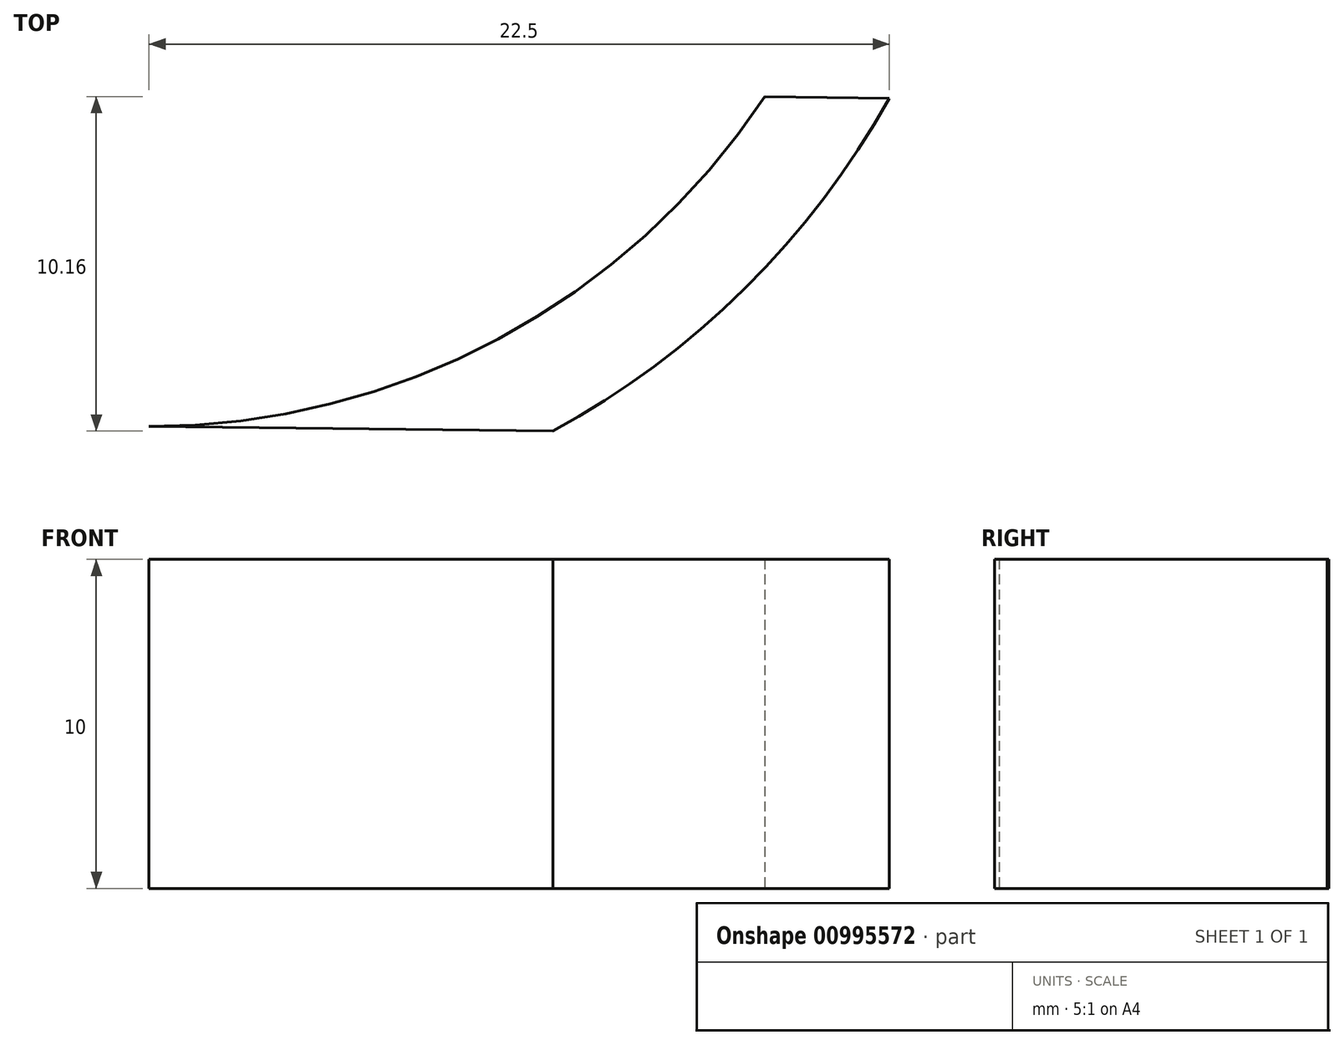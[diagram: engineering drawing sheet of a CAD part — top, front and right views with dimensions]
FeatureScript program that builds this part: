
annotation { "Feature Type Name" : "Feature", "Feature Type Description" : "" }
export const myFeature = defineFeature(function(context is Context, id is Id, definition is map)
    precondition{}
    {
        {
            var Q0;
            Q0=qCreatedBy(makeId("Top.planeOp"),FACE);
            var sketch = newSketch(context, id + "F0", { "sketchPlane" : qUnion([Q0])});
            skLineSegment(sketch, "E0", {"start": v(-15.96, 20.32) * mm, "end": v(-15.96, -25.18) * mm, "construction": true});
            skPoint(sketch, "E1", {"position": v(-15.96, -2.43) * mm});
            skLineSegment(sketch, "E2", {"start": v(70.17, -2.43) * mm, "end": v(-91.58, -2.43) * mm, "construction": true});
            skLineSegment(sketch, "E3", {"start": v(-15.96, -2.43) * mm, "end": v(-38.46, -2.43) * mm, "construction": true});
            skCircle(sketch, "E4", {"center": v(-38.46, -2.43) * mm, "radius": 22.5 * mm, "construction": true});
            skLineSegment(sketch, "E5", {"start": v(-38.46, -2.43) * mm, "end": v(-38.46, 20.07) * mm, "construction": true});
            skLineSegment(sketch, "E6", {"start": v(-38.46, -2.43) * mm, "end": v(-38.46, -24.93) * mm, "construction": true});
            skArc(sketch, "E7", {"start": v(-38.46, 23.32) * mm, "mid": v(-56.67, 15.77) * mm, "end": v(-64.21, -2.43) * mm});
            skArc(sketch, "E8", {"start": v(-38.46, 20.07) * mm, "mid": v(-54.37, 13.48) * mm, "end": v(-60.96, -2.43) * mm});
            skArc(sketch, "E9", {"start": v(-38.46, 23.32) * mm, "mid": v(-32.13, 22.53) * mm, "end": v(-26.2, 20.2) * mm, "construction": true});
            skArc(sketch, "E10", {"start": v(-26.2, 20.2) * mm, "mid": v(-20.36, 15.87) * mm, "end": v(-15.96, 10.09) * mm});
            skLineSegment(sketch, "E11", {"start": v(-15.96, 10.09) * mm, "end": v(-19.74, 10.05) * mm});
            skArc(sketch, "E12", {"start": v(-38.46, 20.07) * mm, "mid": v(-27.85, 17.4) * mm, "end": v(-19.74, 10.05) * mm});
            skArc(sketch, "E13.MirrorCS", {"start": v(-38.46, -28.18) * mm, "mid": v(-56.67, -20.64) * mm, "end": v(-64.21, -2.43) * mm});
            skArc(sketch, "E14.MirrorCS", {"start": v(-38.46, -24.93) * mm, "mid": v(-54.37, -18.34) * mm, "end": v(-60.96, -2.43) * mm});
            skArc(sketch, "E15.MirrorCS", {"start": v(-38.46, -24.93) * mm, "mid": v(-27.85, -22.27) * mm, "end": v(-19.74, -14.91) * mm});
            skLineSegment(sketch, "E16.MirrorCS", {"start": v(4.39, -28.18) * mm, "end": v(-38.46, -28.18) * mm});
            skArc(sketch, "E17.MirrorCS", {"start": v(-26.2, -25.07) * mm, "mid": v(-20.36, -20.74) * mm, "end": v(-15.96, -14.96) * mm});
            skLineSegment(sketch, "E18.MirrorCS", {"start": v(-15.96, -25.18) * mm, "end": v(-38.46, -24.93) * mm});
            skLineSegment(sketch, "E19.MirrorCS", {"start": v(-15.96, -14.96) * mm, "end": v(-19.74, -14.91) * mm});
            skLineSegment(sketch, "E20.MirrorCS", {"start": v(1.04, -25.18) * mm, "end": v(-15.96, -25.18) * mm});
            skLineSegment(sketch, "E21.MirrorCS", {"start": v(1.04, -22.18) * mm, "end": v(1.04, -25.18) * mm});
            skLineSegment(sketch, "E22.MirrorCS", {"start": v(4.39, -25.18) * mm, "end": v(1.04, -22.18) * mm});
            skLineSegment(sketch, "E23.MirrorCS", {"start": v(4.39, -28.18) * mm, "end": v(4.39, -25.18) * mm});
            skLineSegment(sketch, "E24", {"start": v(1.04, 20.32) * mm, "end": v(70.17, 20.32) * mm, "construction": true});
            skLineSegment(sketch, "E25.MirrorCS", {"start": v(4.39, 65.82) * mm, "end": v(1.04, 62.82) * mm});
            skLineSegment(sketch, "E26.MirrorCS", {"start": v(1.04, 65.82) * mm, "end": v(-15.96, 65.82) * mm});
            skLineSegment(sketch, "E27.MirrorCS", {"start": v(4.39, 68.82) * mm, "end": v(4.39, 65.82) * mm});
            skLineSegment(sketch, "E28", {"start": v(1.04, 65.82) * mm, "end": v(1.04, -25.18) * mm, "construction": true});
            skLineSegment(sketch, "E29", {"start": v(1.04, 65.82) * mm, "end": v(1.04, 62.82) * mm});
            skLineSegment(sketch, "E30", {"start": v(4.39, 68.82) * mm, "end": v(-15.96, 68.82) * mm});
            skLineSegment(sketch, "E31", {"start": v(-15.96, 68.82) * mm, "end": v(-18.96, 68.82) * mm});
            skLineSegment(sketch, "E32", {"start": v(-18.96, 68.82) * mm, "end": v(-18.96, 23.32) * mm});
            skLineSegment(sketch, "E33", {"start": v(-15.96, 65.82) * mm, "end": v(-15.96, 20.32) * mm});
            skLineSegment(sketch, "E34", {"start": v(-15.96, 20.32) * mm, "end": v(-26.2, 20.2) * mm});
            skLineSegment(sketch, "E35", {"start": v(-18.96, 23.32) * mm, "end": v(-38.46, 23.32) * mm});
            skSolve(sketch);
        }
        {
            var Q0;
            Q0=makeQuery(id+"F0.imprint","IMPRINT",FACE,{"disambiguationData":[TD([[makeQuery(id+"F0.imprint","IMPRINT",EDGE,{"derivedFrom":sQuery(id+"F0.wireOp",EDGE,"1zlO5T9E-C2hf-zUbD-L893-QL6VvcpCyhPs")}),-1.0]])]});
            var Q1;
            {var subQ2=sQuery(id+"F0.wireOp",EDGE,"E10");Q1=makeQuery(id+"F0.imprint","IMPRINT",FACE,{"disambiguationData":[TD([[makeQuery(id+"F0.imprint","IMPRINT",EDGE,{"derivedFrom":subQ2}),-1.0]])]});}
            var Q2;
            {var subQ0=sQuery(id+"F0.wireOp",EDGE,"E15.MirrorCS");Q2=makeQuery(id+"F0.imprint","IMPRINT",FACE,{"disambiguationData":[TD([[makeQuery(id+"F0.imprint","IMPRINT",EDGE,{"derivedFrom":subQ0}),-1.0]])]});}
            extrude(context, id + "F1", {"entities" : qUnion([Q0, Q1, Q2]), "depth" : 10 * mm, "offsetDistance" : 25 * mm});
        }
    });
